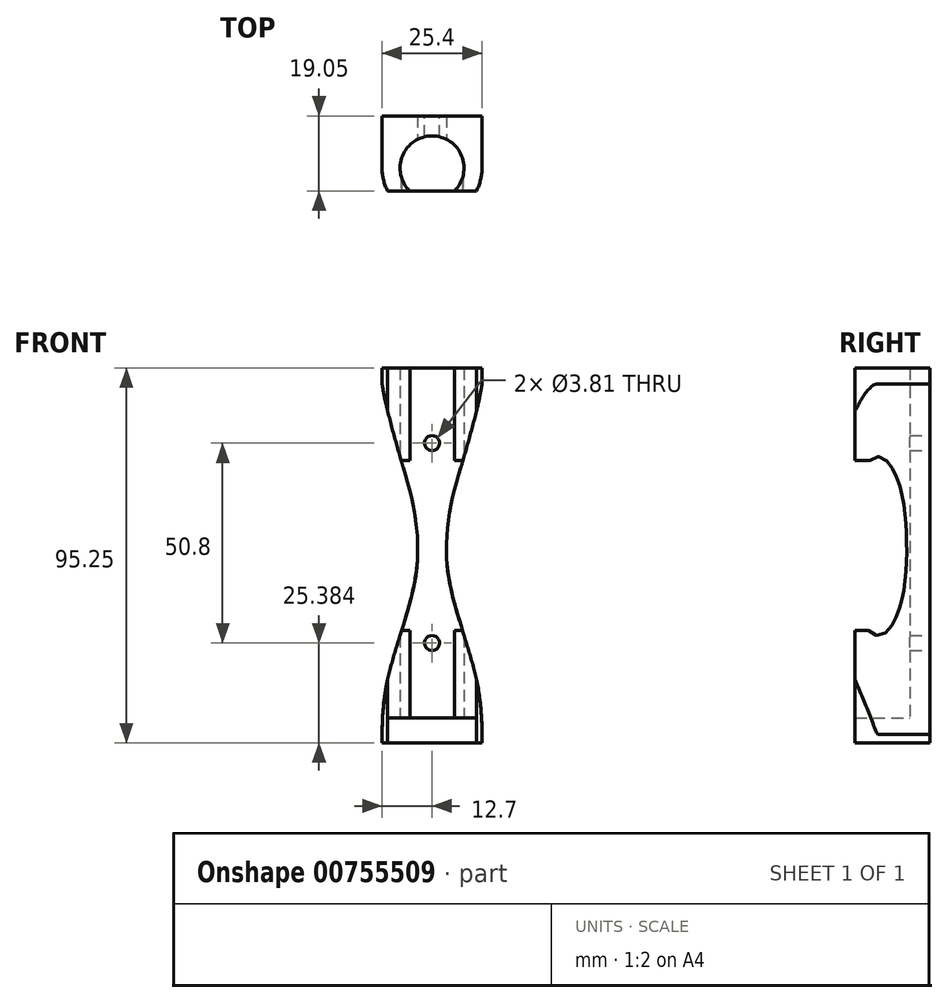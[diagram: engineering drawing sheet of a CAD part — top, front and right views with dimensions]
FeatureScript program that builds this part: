
annotation { "Feature Type Name" : "Feature", "Feature Type Description" : "" }
export const myFeature = defineFeature(function(context is Context, id is Id, definition is map)
    precondition{}
    {
        {
            var Q0;
            Q0=qCreatedBy(makeId("Front.planeOp"),FACE);
            var sketch = newSketch(context, id + "F0", { "sketchPlane" : qUnion([Q0])});
            skLineSegment(sketch, "E0.bottom", {"start": v(0, 0) * mm, "end": v(25.4, 0) * mm});
            skLineSegment(sketch, "E0.top", {"start": v(0, 88.9) * mm, "end": v(25.4, 88.9) * mm});
            skLineSegment(sketch, "E0.left", {"start": v(0, 0) * mm, "end": v(0, 88.9) * mm});
            skLineSegment(sketch, "E0.right", {"start": v(25.4, 0) * mm, "end": v(25.4, 88.9) * mm});
            skSolve(sketch);
        }
        {
            var Q0;
            Q0 = qSketchRegion(id + "F0", true);
            extrude(context, id + "F1", {"entities" : qUnion([Q0]), "depth" : 19.05 * mm, "offsetDistance" : 25.4 * mm});
        }
        {
            var Q0;
            Q0=makeQuery(id+"F1.opExtrude","SWEPT_FACE",FACE,{"disambiguationData":[OSD([sQuery(id+"F0.wireOp",EDGE,"E0.bottom")])]});
            var sketch = newSketch(context, id + "F2", { "sketchPlane" : qUnion([Q0])});
            skCircle(sketch, "E1", {"center": v(12.7, 13.2) * mm, "radius": 8.13 * mm});
            skSolve(sketch);
        }
        {
            var Q0;
            {var subQ0=sQuery(id+"F2.wireOp",EDGE,"E1");var subQ1=makeQuery(id+"F1.opExtrude","CAP_EDGE",EDGE,{"disambiguationData":[OSD([sQuery(id+"F0.wireOp",EDGE,"E0.bottom")])],"isStart":false});var subQ2=makeQuery(id+"F2.imprint","INTERSECT",VERTEX,{"disambiguationData":[OD(0.0)],"derivedFrom":[subQ1,subQ0]});Q0=makeQuery(id+"F2.imprint","IMPRINT",FACE,{"disambiguationData":[TD([[makeQuery(id+"F2.imprint","IMPRINT",EDGE,{"disambiguationData":[TD([[subQ2,-1.0]])],"derivedFrom":subQ0}),1.0]])]});}
            var Q1;
            Q1=sQuery(id+"F2.wireOp",EDGE,"E1");
            extrude(context, id + "F3", {"entities" : qUnion([Q0]), "operationType" : NewBodyOperationType.REMOVE, "surfaceEntities" : qUnion([Q1]), "oppositeDirection" : true, "depth" : 88.9 * mm, "offsetDistance" : 25.4 * mm});
        }
        {
            var Q0;
            Q0=makeQuery(id+"F1.opExtrude","SWEPT_FACE",FACE,{"disambiguationData":[OSD([sQuery(id+"F0.wireOp",EDGE,"E0.bottom")])]});
            var sketch = newSketch(context, id + "F4", { "sketchPlane" : qUnion([Q0])});
            skLineSegment(sketch, "E2.bottom", {"start": v(0, 0) * mm, "end": v(25.4, 0) * mm});
            skLineSegment(sketch, "E2.top", {"start": v(0, 19.04) * mm, "end": v(25.4, 19.04) * mm});
            skLineSegment(sketch, "E2.left", {"start": v(0, 0) * mm, "end": v(0, 19.04) * mm});
            skLineSegment(sketch, "E2.right", {"start": v(25.4, 0) * mm, "end": v(25.4, 19.04) * mm});
            skSolve(sketch);
        }
        {
            var Q0;
            Q0 = qSketchRegion(id + "F4", true);
            extrude(context, id + "F5", {"entities" : qUnion([Q0]), "operationType" : NewBodyOperationType.ADD, "depth" : 6.35 * mm, "offsetDistance" : 25.4 * mm});
        }
        {
            var Q0;
            Q0=makeQuery(id+"F1.opExtrude","SWEPT_FACE",FACE,{"disambiguationData":[OSD([sQuery(id+"F0.wireOp",EDGE,"E0.bottom")])]});
            var sketch = newSketch(context, id + "F6", { "sketchPlane" : qUnion([Q0])});
            skArc(sketch, "E3", {"start": v(25.4, 13.2) * mm, "mid": v(12.7, 25.9) * mm, "end": v(0, 13.2) * mm});
            skArc(sketch, "E4", {"start": v(31.75, 13.2) * mm, "mid": v(12.7, 32.26) * mm, "end": v(-6.35, 13.2) * mm});
            skLineSegment(sketch, "E5", {"start": v(0, 13.2) * mm, "end": v(-6.35, 13.2) * mm});
            skLineSegment(sketch, "E6", {"start": v(25.4, 13.2) * mm, "end": v(31.75, 13.2) * mm});
            skSolve(sketch);
        }
        {
            var Q0;
            Q0 = qSketchRegion(id + "F6", true);
            extrude(context, id + "F7", {"entities" : qUnion([Q0]), "operationType" : NewBodyOperationType.REMOVE, "endBound" : BoundingType.SYMMETRIC, "oppositeDirection" : true, "depth" : 228.6 * mm, "offsetDistance" : 25.4 * mm});
        }
        {
            var Q0;
            Q0=makeQuery(id+"F5.boolean.opBoolean","MERGE",FACE,{"derivedFrom":[makeQuery(id+"F1.opExtrude","CAP_FACE",FACE,{"disambiguationData":[OSD([sQuery(id+"F0.wireOp",EDGE,"E0.bottom"),sQuery(id+"F0.wireOp",EDGE,"E0.top"),sQuery(id+"F0.wireOp",EDGE,"E0.left"),sQuery(id+"F0.wireOp",EDGE,"E0.right")])],"isStart":true}),makeQuery(id+"F5.opExtrude","SWEPT_FACE",FACE,{"disambiguationData":[OSD([sQuery(id+"F4.wireOp",EDGE,"E2.bottom")])]})]});
            var sketch = newSketch(context, id + "F8", { "sketchPlane" : qUnion([Q0])});
            skCircle(sketch, "E7", {"center": v(-12.7, 69.83) * mm, "radius": 1.9 * mm});
            skCircle(sketch, "E8.0.1.0", {"center": v(-12.7, 19.03) * mm, "radius": 1.9 * mm});
            skLineSegment(sketch, "E8.direction1", {"start": v(-12.7, 69.83) * mm, "end": v(12.7, 69.83) * mm, "construction": true});
            skLineSegment(sketch, "E8.direction2", {"start": v(-12.7, 69.83) * mm, "end": v(-12.7, 19.03) * mm, "construction": true});
            skSolve(sketch);
        }
        {
            var Q0;
            Q0 = qSketchRegion(id + "F8", true);
            extrude(context, id + "F9", {"entities" : qUnion([Q0]), "operationType" : NewBodyOperationType.REMOVE, "oppositeDirection" : true, "depth" : 25.4 * mm, "offsetDistance" : 25.4 * mm});
        }
        {
            var Q0;
            {var subQ0=sQuery(id+"F0.wireOp",EDGE,"E0.bottom");var subQ1=sQuery(id+"F0.wireOp",EDGE,"E0.top");var subQ2=sQuery(id+"F0.wireOp",EDGE,"E0.left");Q0=makeQuery(id+"F3.boolean.opBoolean","SPLIT",FACE,{"disambiguationData":[TD([makeQuery(id+"F1.opExtrude","SWEPT_FACE",FACE,{"disambiguationData":[OSD([subQ2])]})])],"derivedFrom":makeQuery(id+"F1.opExtrude","CAP_FACE",FACE,{"disambiguationData":[OSD([subQ0,subQ1,subQ2,sQuery(id+"F0.wireOp",EDGE,"E0.right")])],"isStart":false})});}
            var sketch = newSketch(context, id + "F10", { "sketchPlane" : qUnion([Q0])});
            skFitSpline(sketch, "E9", {"points": [v(0, 91.2) * mm, v(0, 84.9) * mm, v(5.67, 62.61) * mm, v(8.1, 53.01) * mm, v(8.57, 36.3) * mm, v(1.42, 9.77) * mm, v(0, -8.88) * mm], "startDerivative": vector(-5.98, -47.98) * mm, "endDerivative": vector(0.6, -98.57) * mm});
            skFitSpline(sketch, "E10.MirrorCS", {"points": [v(25.4, 91.2) * mm, v(25.4, 84.9) * mm, v(19.73, 62.61) * mm, v(17.3, 53.01) * mm, v(16.83, 36.3) * mm, v(23.98, 9.77) * mm, v(25.4, -8.88) * mm], "startDerivative": vector(5.98, -47.98) * mm, "endDerivative": vector(-0.6, -98.57) * mm});
            skLineSegment(sketch, "E11", {"start": v(0, 91.2) * mm, "end": v(25.4, 91.2) * mm});
            skLineSegment(sketch, "E12", {"start": v(0, -8.88) * mm, "end": v(25.4, -8.88) * mm});
            skLineSegment(sketch, "E13.bottom", {"start": v(-3.17, 94.05) * mm, "end": v(29.34, 94.05) * mm});
            skLineSegment(sketch, "E13.top", {"start": v(-3.17, -12.9) * mm, "end": v(29.34, -12.9) * mm});
            skLineSegment(sketch, "E13.left", {"start": v(-3.17, 94.05) * mm, "end": v(-3.17, -12.9) * mm});
            skLineSegment(sketch, "E13.right", {"start": v(29.34, 94.05) * mm, "end": v(29.34, -12.9) * mm});
            skSolve(sketch);
        }
        {
            var Q0;
            Q0 = qSketchRegion(id + "F10", true);
            extrude(context, id + "F11", {"entities" : qUnion([Q0]), "operationType" : NewBodyOperationType.REMOVE, "oppositeDirection" : true, "depth" : 25.4 * mm, "offsetDistance" : 25.4 * mm});
        }
        {
            var Q0;
            {var subQ0=sQuery(id+"F0.wireOp",EDGE,"E0.left");var subQ1=makeQuery(id+"F1.opExtrude","SWEPT_FACE",FACE,{"disambiguationData":[OSD([subQ0])]});var subQ2=sQuery(id+"F0.wireOp",EDGE,"E0.top");var subQ3=makeQuery(id+"F1.opExtrude","SWEPT_FACE",FACE,{"disambiguationData":[OSD([subQ2])]});var subQ4=sQuery(id+"F4.wireOp",EDGE,"E2.left");var subQ5=makeQuery(id+"F5.opExtrude","SWEPT_FACE",FACE,{"disambiguationData":[OSD([subQ4])]});Q0=makeQuery(id+"F11.boolean.opBoolean","SPLIT",FACE,{"disambiguationData":[TD([subQ3])],"derivedFrom":makeQuery(id+"F5.boolean.opBoolean","MERGE",FACE,{"derivedFrom":[subQ1,subQ5]})});}
            var sketch = newSketch(context, id + "F12", { "sketchPlane" : qUnion([Q0])});
            skLineSegment(sketch, "E14.bottom", {"start": v(20.65, 65.43) * mm, "end": v(12.62, 65.43) * mm});
            skLineSegment(sketch, "E14.top", {"start": v(20.65, 22.22) * mm, "end": v(12.62, 22.22) * mm});
            skLineSegment(sketch, "E14.left", {"start": v(20.65, 65.43) * mm, "end": v(20.65, 22.22) * mm});
            skLineSegment(sketch, "E14.right", {"start": v(12.62, 65.43) * mm, "end": v(12.62, 22.22) * mm});
            skSolve(sketch);
        }
        {
            var Q0;
            Q0 = qSketchRegion(id + "F12", true);
            extrude(context, id + "F13", {"entities" : qUnion([Q0]), "operationType" : NewBodyOperationType.REMOVE, "oppositeDirection" : true, "depth" : 25.4 * mm, "offsetDistance" : 25.4 * mm});
        }
    });
